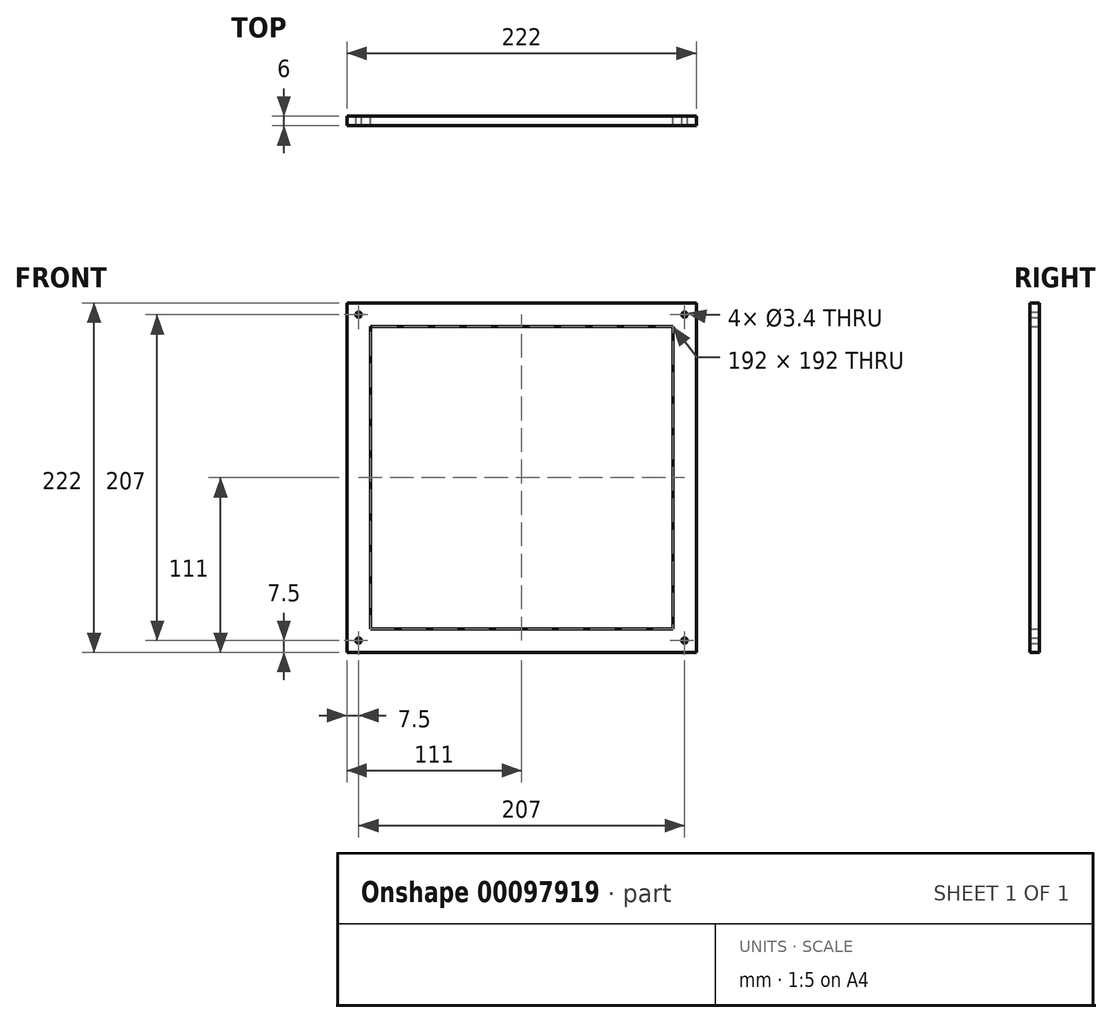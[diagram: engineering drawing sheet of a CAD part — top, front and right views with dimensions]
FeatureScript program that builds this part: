
annotation { "Feature Type Name" : "Feature", "Feature Type Description" : "" }
export const myFeature = defineFeature(function(context is Context, id is Id, definition is map)
    precondition{}
    {
        {
            var Q0;
            Q0=qCreatedBy(makeId("Front.planeOp"),FACE);
            var sketch = newSketch(context, id + "F0", { "sketchPlane" : qUnion([Q0])});
            skLineSegment(sketch, "E0.bottom", {"start": v(-111, 111) * mm, "end": v(111, 111) * mm});
            skLineSegment(sketch, "E0.top", {"start": v(-111, -111) * mm, "end": v(111, -111) * mm});
            skLineSegment(sketch, "E0.left", {"start": v(-111, 111) * mm, "end": v(-111, -111) * mm});
            skLineSegment(sketch, "E0.right", {"start": v(111, 111) * mm, "end": v(111, -111) * mm});
            skLineSegment(sketch, "E1.0", {"start": v(-96, 96) * mm, "end": v(96, 96) * mm});
            skLineSegment(sketch, "E1.1", {"start": v(-96, 96) * mm, "end": v(-96, -96) * mm});
            skLineSegment(sketch, "E1.2", {"start": v(-96, -96) * mm, "end": v(96, -96) * mm});
            skLineSegment(sketch, "E1.3", {"start": v(96, 96) * mm, "end": v(96, -96) * mm});
            skCircle(sketch, "E2", {"center": v(-103.5, 103.5) * mm, "radius": 1.7 * mm});
            skCircle(sketch, "E3.0.1.0", {"center": v(-103.5, -103.5) * mm, "radius": 1.7 * mm});
            skCircle(sketch, "E3.1.0.0", {"center": v(103.5, 103.5) * mm, "radius": 1.7 * mm});
            skCircle(sketch, "E3.1.1.0", {"center": v(103.5, -103.5) * mm, "radius": 1.7 * mm});
            skLineSegment(sketch, "E3.direction1", {"start": v(-103.5, 103.5) * mm, "end": v(103.5, 103.5) * mm, "construction": true});
            skLineSegment(sketch, "E3.direction2", {"start": v(-103.5, 103.5) * mm, "end": v(-103.5, -103.5) * mm, "construction": true});
            skSolve(sketch);
        }
        {
            var Q0;
            Q0=makeQuery(id+"F0.imprint","IMPRINT",FACE,{"disambiguationData":[TD([[makeQuery(id+"F0.imprint","IMPRINT",EDGE,{"derivedFrom":sQuery(id+"F0.wireOp",EDGE,"E0.bottom")}),-1.0]])]});
            extrude(context, id + "F1", {"entities" : qUnion([Q0]), "depth" : 6 * mm});
        }
    });
